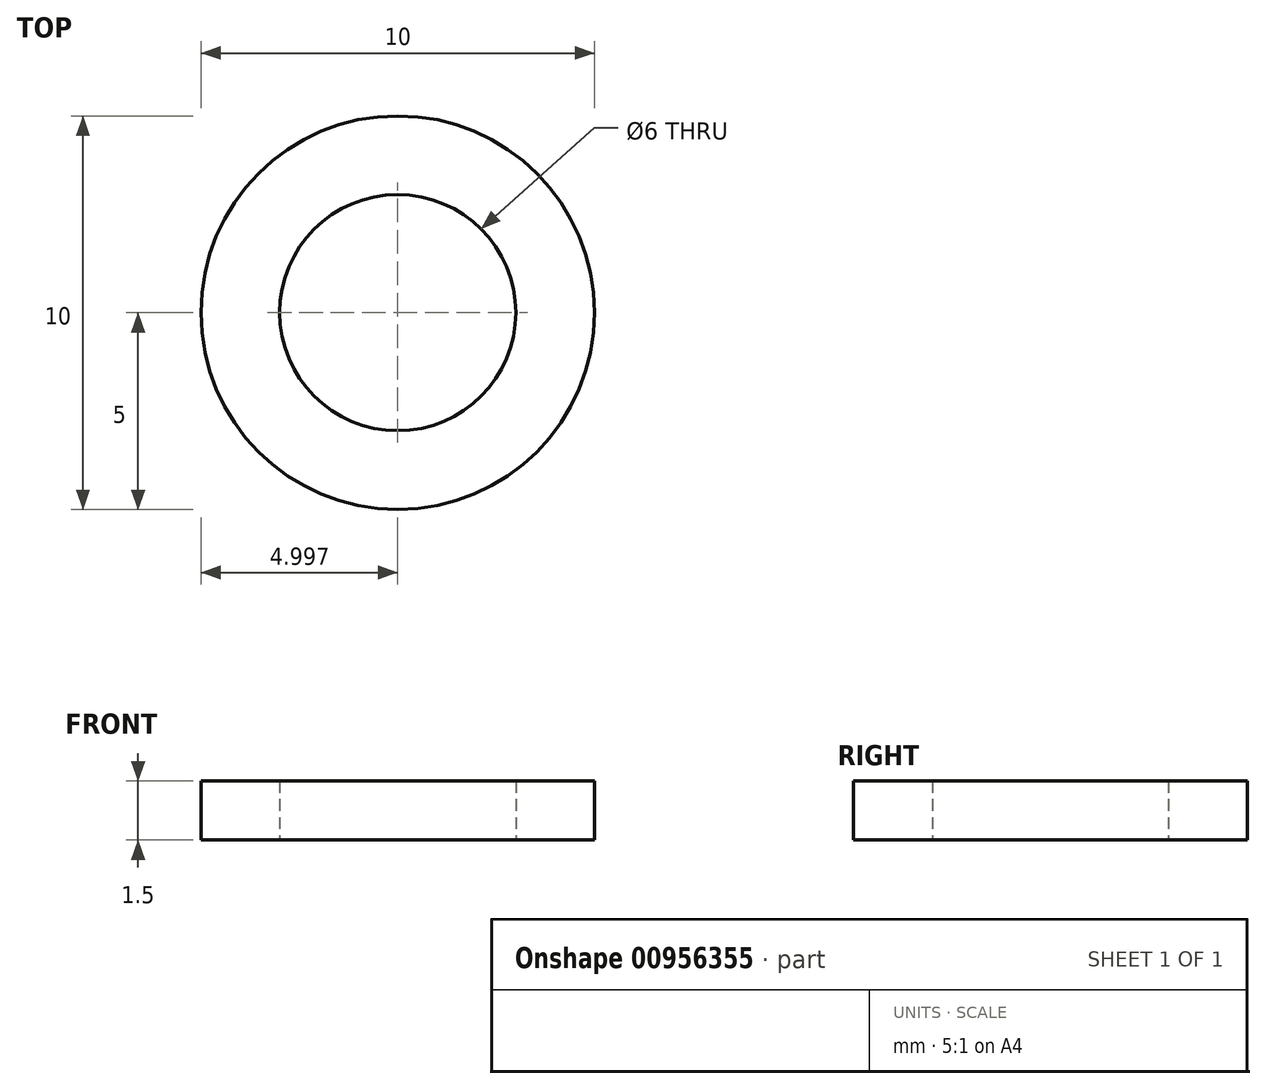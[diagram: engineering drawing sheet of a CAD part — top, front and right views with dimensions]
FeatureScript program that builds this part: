
annotation { "Feature Type Name" : "Feature", "Feature Type Description" : "" }
export const myFeature = defineFeature(function(context is Context, id is Id, definition is map)
    precondition{}
    {
        {
            var Q0;
            Q0=qCreatedBy(makeId("Top.planeOp"),FACE);
            var sketch = newSketch(context, id + "F0", { "sketchPlane" : qUnion([Q0])});
            skCircle(sketch, "E0", {"center": v(-26.33, 0) * mm, "radius": 3 * mm});
            skCircle(sketch, "E1", {"center": v(-26.33, 0) * mm, "radius": 5 * mm});
            skSolve(sketch);
        }
        {
            var Q0;
            Q0=makeQuery(id+"F0.imprint","IMPRINT",FACE,{"disambiguationData":[TD([[makeQuery(id+"F0.imprint","IMPRINT",EDGE,{"derivedFrom":sQuery(id+"F0.wireOp",EDGE,"E0")}),-1.0]])]});
            extrude(context, id + "F1", {"entities" : qUnion([Q0]), "depth" : 1.5 * mm, "offsetDistance" : 25.4 * mm});
        }
    });
